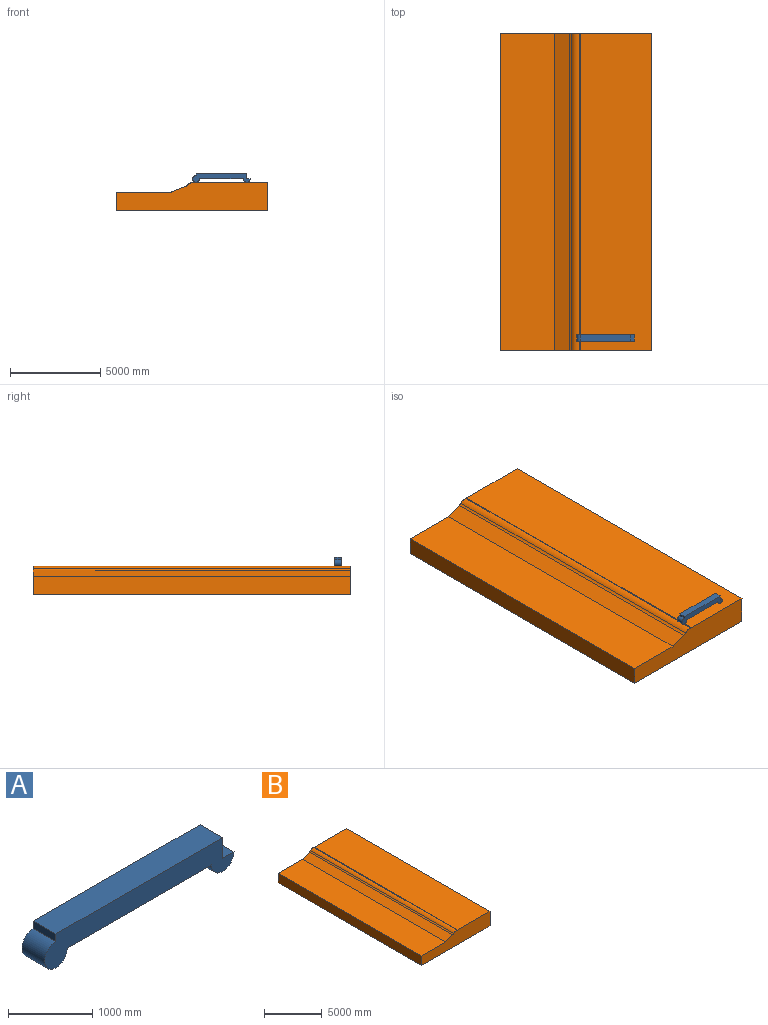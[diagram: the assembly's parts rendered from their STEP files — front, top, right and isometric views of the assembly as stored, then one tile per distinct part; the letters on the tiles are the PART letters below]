
ASSEMBLY  parts=2 mates=1
PART A: 9 faces, bbox 3181x378.5x490.5 mm
  f0: plane 2419x378.51mm, normal (0,0,-1), area 915623.3mm2, adj f1,f6,f7,f8
  f1: cylinder r=190.5mm len=381mm, axis (0,1,0), area 226340.7mm2, adj f0,f2,f7,f8
  f2: plane 378.51x190.5mm, normal (0,0,1), area 72106.7mm2, adj f1,f3,f7,f8
  f3: plane 378.51x300mm, normal (1,0,0), area 113553.9mm2, adj f2,f4,f7,f8
  f4: plane 2800x378.51mm, normal (0,0,1), area 1059836.3mm2, adj f3,f5,f7,f8
  f5: plane 378.51x109.5mm, normal (-1,0,0), area 41447.2mm2, adj f4,f6,f7,f8
  f6: cylinder r=190.5mm len=381mm, axis (0,1,0), area 339605.6mm2, adj f0,f5,f7,f8
  f7: plane 3181x490.5mm, normal (0,-1,0), area 983721mm2, adj f0,f1,f2,f3,f4,f5,f6
  f8: plane 3181x490.5mm, normal (0,1,0), area 983721mm2, adj f0,f1,f2,f3,f4,f5,f6
PART B: 11 faces, bbox 8392.7x17562.8x1563.9 mm
  f0: cylinder r=479.17mm len=17562.82mm, axis (0,-1,0), area 7638097.6mm2, adj f7,f8,f9,f10
  f1: plane 17562.82x840.56mm, normal (-0.37,0,0.93), area 15899834.3mm2, adj f2,f7,f8,f9
  f2: plane 17562.82x3000mm, normal (0,0,1), area 52688461.3mm2, adj f1,f3,f7,f8
  f3: plane 17562.82x1000mm, normal (-1,0,0), area 17562820.4mm2, adj f2,f4,f7,f8
  f4: plane 17562.82x8392.72mm, normal (0,0,-1), area 147399747.1mm2, adj f3,f5,f7,f8
  f5: plane 17562.82x1557.09mm, normal (1,0,0), area 27346822.1mm2, adj f4,f6,f7,f8
  f6: plane 17562.82x3971.35mm, normal (0,0,1), area 69748166.9mm2, adj f5,f7,f8,f10
  f7: plane 8392.72x1563.86mm, normal (0,1,0), area 11033429.2mm2, adj f0,f1,f2,f3,f4,f5,f6,f9
  f8: plane 8392.72x1563.86mm, normal (0,-1,0), area 11033429.2mm2, adj f0,f1,f2,f3,f4,f5,f6,f9
  f9: cylinder r=400mm len=17562.82mm, axis (0,-1,0), area 2830227.8mm2, adj f0,f1,f7,f8
  f10: cylinder r=400mm len=17562.82mm, axis (0,-1,0), area 872818.1mm2, adj f0,f6,f7,f8
PLACE A rot(axis=(0.87,0.48,-0.09),0deg) t=(9378.46,883.29,2094.85)mm
PLACE B rot(axis=(0.88,0.47,-0.09),0deg) t=(8369.34,-15.28,1824.55)mm fixed
MATE parallel A.f7 <-> B.f8  axis (0,-1,0) through (9795.28,504.69,2314.98)mm
